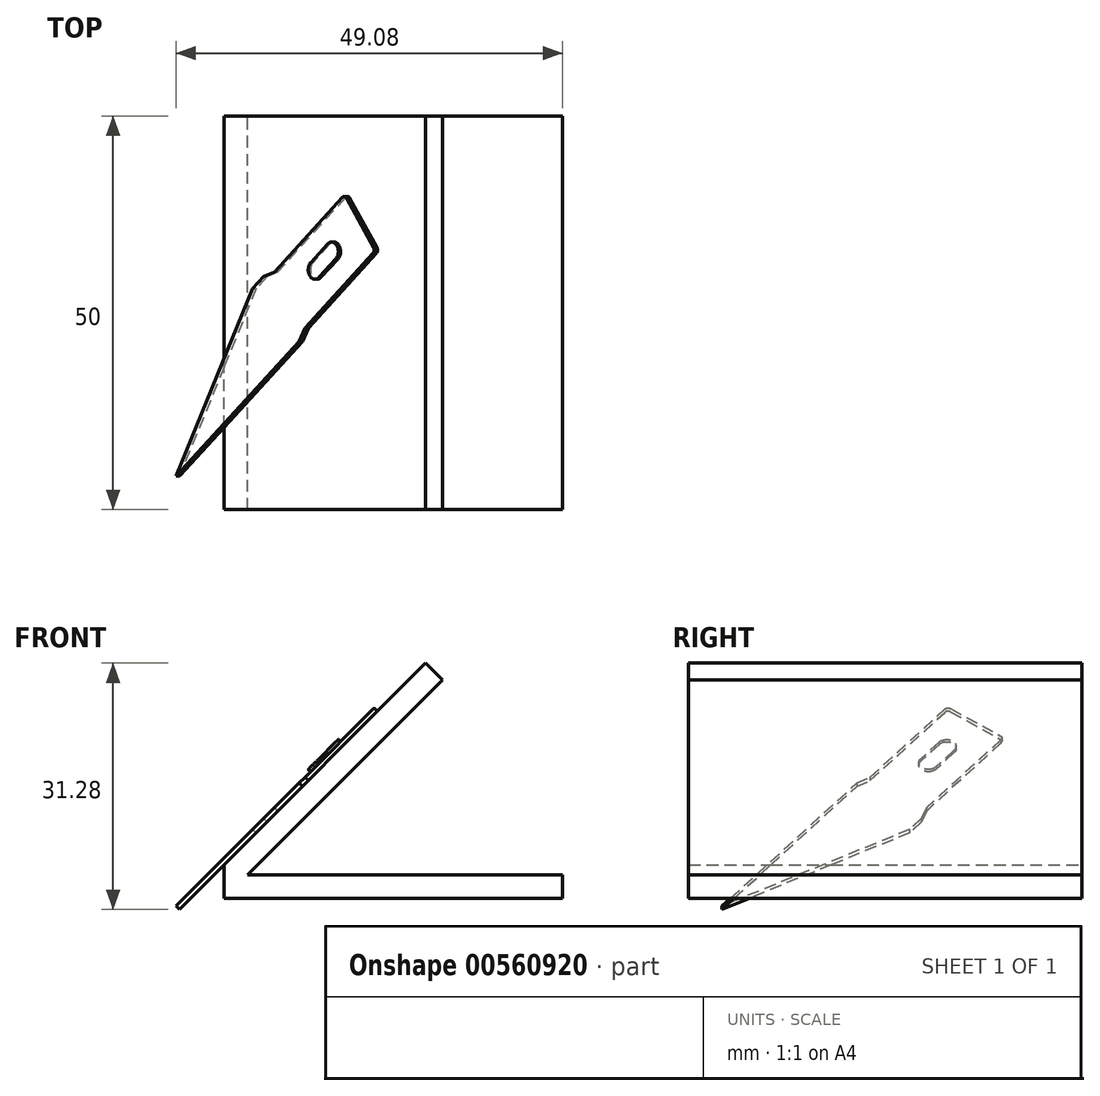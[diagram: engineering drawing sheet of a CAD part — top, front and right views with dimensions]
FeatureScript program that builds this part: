
annotation { "Feature Type Name" : "Feature", "Feature Type Description" : "" }
export const myFeature = defineFeature(function(context is Context, id is Id, definition is map)
    precondition{}
    {
        {
            var Q0;
            Q0=qCreatedBy(makeId("Front.planeOp"),FACE);
            var sketch = newSketch(context, id + "F0", { "sketchPlane" : qUnion([Q0])});
            skLineSegment(sketch, "E0", {"start": v(45.75, 3) * mm, "end": v(5.75, 3) * mm});
            skLineSegment(sketch, "E1", {"start": v(5.75, 3) * mm, "end": v(30.5, 27.75) * mm});
            skLineSegment(sketch, "E2", {"start": v(30.5, 27.75) * mm, "end": v(28.38, 29.87) * mm});
            skLineSegment(sketch, "E3", {"start": v(28.38, 29.87) * mm, "end": v(2.75, 4.24) * mm});
            skLineSegment(sketch, "E4", {"start": v(2.75, 4.24) * mm, "end": v(2.75, 0) * mm});
            skLineSegment(sketch, "E5", {"start": v(2.75, 0) * mm, "end": v(45.75, 0) * mm});
            skLineSegment(sketch, "E6", {"start": v(45.75, 0) * mm, "end": v(45.75, 3) * mm});
            skSolve(sketch);
        }
        {
            var Q0;
            Q0=makeQuery(id+"F0.imprint","IMPRINT",FACE,{"disambiguationData":[TD([[makeQuery(id+"F0.imprint","IMPRINT",EDGE,{"derivedFrom":sQuery(id+"F0.wireOp",EDGE,"E0")}),1.0]])]});
            extrude(context, id + "F1", {"entities" : qUnion([Q0]), "depth" : 50 * mm, "offsetDistance" : 25 * mm});
        }
        {
            var Q0;
            Q0=makeQuery(id+"F1.opExtrude","SWEPT_FACE",FACE,{"disambiguationData":[OSD([sQuery(id+"F0.wireOp",EDGE,"E3")])]});
            var sketch = newSketch(context, id + "F2", { "sketchPlane" : qUnion([Q0])});
            skLineSegment(sketch, "E7", {"start": v(26.92, 20.1) * mm, "end": v(17.11, 32.74) * mm});
            skLineSegment(sketch, "E8", {"start": v(17.11, 32.74) * mm, "end": v(10, 27.23) * mm});
            skLineSegment(sketch, "E9", {"start": v(10, 27.23) * mm, "end": v(19.8, 14.58) * mm});
            skLineSegment(sketch, "E10", {"start": v(19.8, 14.58) * mm, "end": v(20.4, 12.67) * mm});
            skLineSegment(sketch, "E11", {"start": v(45.74, -3.05) * mm, "end": v(28.62, 19.04) * mm});
            skLineSegment(sketch, "E12", {"start": v(28.62, 19.04) * mm, "end": v(26.92, 20.1) * mm});
            skLineSegment(sketch, "E13", {"start": v(20.4, 12.67) * mm, "end": v(21.93, 10.7) * mm});
            skLineSegment(sketch, "E14", {"start": v(21.93, 10.7) * mm, "end": v(45.74, -3.05) * mm});
            skCircle(sketch, "E15", {"center": v(17.2, 25.28) * mm, "radius": 1.2 * mm});
            skCircle(sketch, "E16", {"center": v(19.53, 22.28) * mm, "radius": 1.2 * mm});
            skLineSegment(sketch, "E17", {"start": v(18.15, 26.02) * mm, "end": v(20.48, 23.01) * mm});
            skLineSegment(sketch, "E18", {"start": v(16.25, 24.55) * mm, "end": v(18.58, 21.54) * mm});
            skSolve(sketch);
        }
        {
            var Q0;
            Q0=makeQuery(id+"F2.imprint","IMPRINT",FACE,{"disambiguationData":[TD([[makeQuery(id+"F2.imprint","IMPRINT",EDGE,{"derivedFrom":sQuery(id+"F2.wireOp",EDGE,"E7")}),1.0]])]});
            var Q1;
            {var subQ0=sQuery(id+"F2.wireOp",EDGE,"E14");var subQ1=sQuery(id+"F2.wireOp",EDGE,"E11");var subQ2=makeQuery(id+"F2.imprint","INTERSECT",VERTEX,{"derivedFrom":[subQ1,subQ0]});Q1=makeQuery(id+"F2.imprint","IMPRINT",FACE,{"disambiguationData":[TD([[makeQuery(id+"F2.imprint","IMPRINT",EDGE,{"disambiguationData":[TD([[subQ2,-1.0]])],"derivedFrom":subQ1}),1.0]])]});}
            extrude(context, id + "F3", {"entities" : qUnion([Q0, Q1]), "operationType" : NewBodyOperationType.ADD, "depth" : 0.6 * mm, "offsetDistance" : 25 * mm});
        }
        {
            var Q0;
            Q0=makeQuery(id+"F3.opExtrude","SWEPT_EDGE",EDGE,{"disambiguationData":[OSD([sQuery(id+"F2.wireOp",EDGE,"E7"),sQuery(id+"F2.wireOp",EDGE,"E8")])]});
            var Q1;
            Q1=makeQuery(id+"F3.opExtrude","SWEPT_EDGE",EDGE,{"disambiguationData":[OSD([sQuery(id+"F2.wireOp",EDGE,"E8"),sQuery(id+"F2.wireOp",EDGE,"E9")])]});
            fillet(context, id + "F4", {"entities" : qUnion([Q0, Q1]), "radius" : 0.5 * mm, "tangentPropagation" : true, "allowEdgeOverflow" : false});
        }
        {
            var Q0;
            {var subQ0=sQuery(id+"F2.wireOp",EDGE,"E17");Q0=makeQuery(id+"F2.imprint","IMPRINT",FACE,{"disambiguationData":[TD([[makeQuery(id+"F2.imprint","IMPRINT",EDGE,{"derivedFrom":subQ0}),-1.0]])]});}
            var Q1;
            {var subQ0=sQuery(id+"F2.wireOp",EDGE,"E15");var subQ1=makeQuery(id+"F2.imprint","INTERSECT",VERTEX,{"derivedFrom":[subQ0,sQuery(id+"F2.wireOp",EDGE,"E17")]});Q1=makeQuery(id+"F2.imprint","IMPRINT",FACE,{"disambiguationData":[TD([[makeQuery(id+"F2.imprint","IMPRINT",EDGE,{"disambiguationData":[TD([[subQ1,-1.0]])],"derivedFrom":subQ0}),1.0]])]});}
            var Q2;
            {var subQ0=sQuery(id+"F2.wireOp",EDGE,"E16");var subQ1=makeQuery(id+"F2.imprint","INTERSECT",VERTEX,{"derivedFrom":[subQ0,sQuery(id+"F2.wireOp",EDGE,"E17")]});Q2=makeQuery(id+"F2.imprint","IMPRINT",FACE,{"disambiguationData":[TD([[makeQuery(id+"F2.imprint","IMPRINT",EDGE,{"disambiguationData":[TD([[subQ1,-1.0]])],"derivedFrom":subQ0}),1.0]])]});}
            extrude(context, id + "F5", {"entities" : qUnion([Q0, Q1, Q2]), "operationType" : NewBodyOperationType.ADD, "depth" : 2 * mm, "offsetDistance" : 25 * mm, "symmetric" : true});
        }
    });
